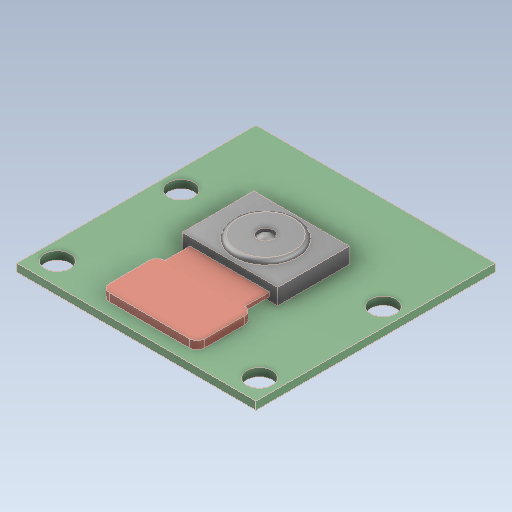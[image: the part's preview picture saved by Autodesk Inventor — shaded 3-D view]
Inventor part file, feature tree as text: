
AUTODESK INVENTOR PART (.ipt)
format: ipt  version: 2021 (Build 250183000, 183)  size: 158,208 bytes
history: mixed  units: mm
features: other x1, revolve x1, imported_body x1
ambient origin geometry x8: Origin, YZ Plane, XZ Plane, XY Plane, X Axis, Y Axis, Z Axis, Center Point
bodies: Body1 (imported_parasolid)
feature tree (3):
  other  "Sólido1"
  revolve  "Revolución1"  [1 undecoded]
  imported_body  NMx_Import_Brep_tag  [imported B-rep: ~6 faces, bbox_mm=None]
note: 1 required parameter value undecoded (feature->parameter linkage not recoverable at this tier; creation-order binding heuristic only, values carry confidence <= 0.55)
